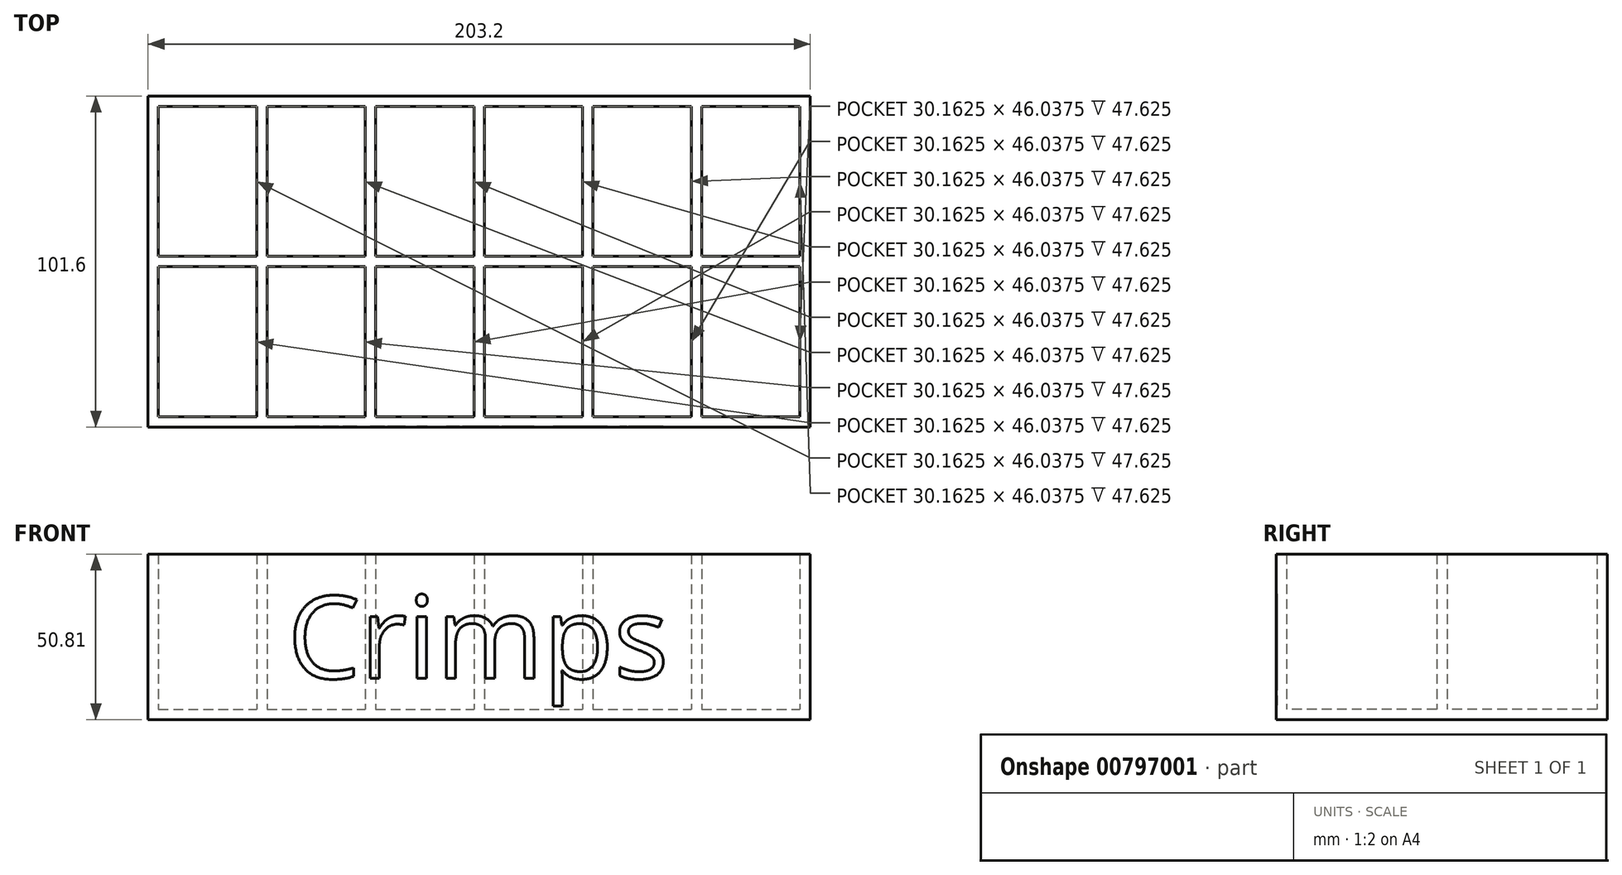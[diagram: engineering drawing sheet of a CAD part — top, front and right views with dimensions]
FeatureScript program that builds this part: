
annotation { "Feature Type Name" : "Feature", "Feature Type Description" : "" }
export const myFeature = defineFeature(function(context is Context, id is Id, definition is map)
    precondition{}
    {
        {
            var Q0;
            Q0=qCreatedBy(makeId("Top.planeOp"),FACE);
            var sketch = newSketch(context, id + "F0", { "sketchPlane" : qUnion([Q0])});
            skLineSegment(sketch, "E0.top", {"start": v(0, -101.6) * mm, "end": v(203.2, -101.6) * mm});
            skLineSegment(sketch, "E0.left", {"start": v(0, 0) * mm, "end": v(0, -101.6) * mm});
            skLineSegment(sketch, "E0.right", {"start": v(203.2, 0) * mm, "end": v(203.2, -101.6) * mm});
            skLineSegment(sketch, "E1.left", {"start": v(3.18, -3.17) * mm, "end": v(3.18, -49.21) * mm});
            skLineSegment(sketch, "E1.right", {"start": v(200.03, -3.17) * mm, "end": v(200.03, -98.43) * mm});
            skLineSegment(sketch, "E2", {"start": v(3.17, -3.17) * mm, "end": v(33.34, -3.17) * mm});
            skLineSegment(sketch, "E3", {"start": v(203.2, 0) * mm, "end": v(0, 0) * mm});
            skLineSegment(sketch, "E4", {"start": v(3.18, -98.43) * mm, "end": v(200.03, -98.43) * mm});
            skLineSegment(sketch, "E5.top", {"start": v(18.18, -98.43) * mm, "end": v(18.18, -98.43) * mm});
            skLineSegment(sketch, "E6", {"start": v(33.34, -98.43) * mm, "end": v(33.34, -52.39) * mm});
            skLineSegment(sketch, "E7", {"start": v(36.51, -3.17) * mm, "end": v(36.51, -3.17) * mm});
            skLineSegment(sketch, "E8", {"start": v(36.51, -3.17) * mm, "end": v(36.51, -49.21) * mm});
            skLineSegment(sketch, "E9", {"start": v(36.51, -3.18) * mm, "end": v(66.67, -3.18) * mm});
            skLineSegment(sketch, "E10", {"start": v(66.68, -98.42) * mm, "end": v(66.68, -3.18) * mm});
            skLineSegment(sketch, "E11", {"start": v(69.85, -3.18) * mm, "end": v(69.85, -49.21) * mm});
            skLineSegment(sketch, "E12", {"start": v(69.85, -3.17) * mm, "end": v(100.01, -3.17) * mm});
            skLineSegment(sketch, "E13", {"start": v(100.01, -3.17) * mm, "end": v(100.01, -98.42) * mm});
            skLineSegment(sketch, "E14", {"start": v(103.19, -3.17) * mm, "end": v(103.19, -49.21) * mm});
            skLineSegment(sketch, "E15", {"start": v(117.07, -3.17) * mm, "end": v(133.35, -3.17) * mm});
            skLineSegment(sketch, "E16", {"start": v(133.35, -3.17) * mm, "end": v(133.35, -98.42) * mm});
            skLineSegment(sketch, "E17", {"start": v(103.19, -3.17) * mm, "end": v(117.07, -3.17) * mm});
            skLineSegment(sketch, "E18", {"start": v(136.52, -3.17) * mm, "end": v(136.53, -49.21) * mm});
            skLineSegment(sketch, "E19", {"start": v(133.35, -3.17) * mm, "end": v(133.35, -3.17) * mm});
            skLineSegment(sketch, "E20", {"start": v(136.52, -3.17) * mm, "end": v(166.69, -3.17) * mm});
            skLineSegment(sketch, "E21", {"start": v(166.69, -3.17) * mm, "end": v(166.69, -98.42) * mm});
            skLineSegment(sketch, "E22", {"start": v(169.86, -3.17) * mm, "end": v(169.86, -49.21) * mm});
            skLineSegment(sketch, "E23", {"start": v(169.86, -3.17) * mm, "end": v(200.03, -3.17) * mm});
            skLineSegment(sketch, "E24", {"start": v(3.18, -49.21) * mm, "end": v(33.34, -49.21) * mm});
            skLineSegment(sketch, "E25", {"start": v(3.18, -52.39) * mm, "end": v(33.34, -52.39) * mm});
            skLineSegment(sketch, "E26", {"start": v(3.18, -49.21) * mm, "end": v(3.18, -52.39) * mm});
            skLineSegment(sketch, "E27", {"start": v(3.18, -52.39) * mm, "end": v(3.18, -98.43) * mm});
            skLineSegment(sketch, "E28", {"start": v(33.34, -49.21) * mm, "end": v(33.34, -3.17) * mm});
            skLineSegment(sketch, "E29", {"start": v(36.51, -49.21) * mm, "end": v(36.51, -49.21) * mm});
            skLineSegment(sketch, "E30", {"start": v(66.68, -52.39) * mm, "end": v(36.51, -52.39) * mm});
            skLineSegment(sketch, "E31", {"start": v(36.51, -49.21) * mm, "end": v(66.68, -49.21) * mm});
            skLineSegment(sketch, "E32", {"start": v(36.51, -52.39) * mm, "end": v(36.51, -98.43) * mm});
            skLineSegment(sketch, "E33", {"start": v(69.85, -49.21) * mm, "end": v(100.01, -49.21) * mm});
            skLineSegment(sketch, "E34", {"start": v(100.01, -52.39) * mm, "end": v(69.85, -52.39) * mm});
            skLineSegment(sketch, "E35", {"start": v(69.85, -52.39) * mm, "end": v(69.85, -52.39) * mm});
            skLineSegment(sketch, "E36", {"start": v(69.85, -52.39) * mm, "end": v(69.85, -98.42) * mm});
            skLineSegment(sketch, "E37", {"start": v(103.19, -49.21) * mm, "end": v(103.19, -49.21) * mm});
            skLineSegment(sketch, "E38", {"start": v(133.35, -52.39) * mm, "end": v(103.19, -52.39) * mm});
            skLineSegment(sketch, "E39", {"start": v(103.19, -49.21) * mm, "end": v(133.35, -49.21) * mm});
            skLineSegment(sketch, "E40", {"start": v(103.19, -52.39) * mm, "end": v(103.19, -98.42) * mm});
            skLineSegment(sketch, "E41", {"start": v(136.53, -49.21) * mm, "end": v(166.69, -49.21) * mm});
            skLineSegment(sketch, "E42", {"start": v(136.53, -52.39) * mm, "end": v(136.53, -52.39) * mm});
            skLineSegment(sketch, "E43", {"start": v(136.53, -52.39) * mm, "end": v(166.69, -52.39) * mm});
            skLineSegment(sketch, "E44", {"start": v(136.53, -52.39) * mm, "end": v(136.53, -98.42) * mm});
            skLineSegment(sketch, "E45", {"start": v(169.86, -49.21) * mm, "end": v(200.03, -49.21) * mm});
            skLineSegment(sketch, "E46", {"start": v(200.03, -52.39) * mm, "end": v(169.86, -52.39) * mm});
            skLineSegment(sketch, "E47", {"start": v(169.86, -52.39) * mm, "end": v(169.86, -98.42) * mm});
            skSolve(sketch);
        }
        {
            var Q0;
            Q0=makeQuery(id+"F0.imprint","IMPRINT",FACE,{"disambiguationData":[TD([[makeQuery(id+"F0.imprint","IMPRINT",EDGE,{"derivedFrom":sQuery(id+"F0.wireOp",EDGE,"E0.top")}),1.0]])]});
            var Q1;
            Q1=makeQuery(id+"F0.imprint","IMPRINT",FACE,{"disambiguationData":[TD([[makeQuery(id+"F0.imprint","IMPRINT",EDGE,{"derivedFrom":sQuery(id+"F0.wireOp",EDGE,"E5.bottom")}),-1.0]])]});
            var Q2;
            {var subQ0=sQuery(id+"F0.wireOp",EDGE,"646c8ae3-f2b2-429d-8022-bc64b3b6f105.1.0.0");Q2=makeQuery(id+"F0.imprint","IMPRINT",FACE,{"disambiguationData":[TD([[makeQuery(id+"F0.imprint","IMPRINT",EDGE,{"derivedFrom":subQ0}),1.0]])]});}
            var Q3;
            {var subQ0=sQuery(id+"F0.wireOp",EDGE,"646c8ae3-f2b2-429d-8022-bc64b3b6f105.2.0.0");Q3=makeQuery(id+"F0.imprint","IMPRINT",FACE,{"disambiguationData":[TD([[makeQuery(id+"F0.imprint","IMPRINT",EDGE,{"derivedFrom":subQ0}),1.0]])]});}
            var Q4;
            {var subQ0=sQuery(id+"F0.wireOp",EDGE,"646c8ae3-f2b2-429d-8022-bc64b3b6f105.3.0.0");Q4=makeQuery(id+"F0.imprint","IMPRINT",FACE,{"disambiguationData":[TD([[makeQuery(id+"F0.imprint","IMPRINT",EDGE,{"derivedFrom":subQ0}),1.0]])]});}
            var Q5;
            {var subQ0=sQuery(id+"F0.wireOp",EDGE,"646c8ae3-f2b2-429d-8022-bc64b3b6f105.4.0.0");Q5=makeQuery(id+"F0.imprint","IMPRINT",FACE,{"disambiguationData":[TD([[makeQuery(id+"F0.imprint","IMPRINT",EDGE,{"derivedFrom":subQ0}),1.0]])]});}
            var Q6;
            {var subQ0=sQuery(id+"F0.wireOp",EDGE,"646c8ae3-f2b2-429d-8022-bc64b3b6f105.5.0.0");Q6=makeQuery(id+"F0.imprint","IMPRINT",FACE,{"disambiguationData":[TD([[makeQuery(id+"F0.imprint","IMPRINT",EDGE,{"derivedFrom":subQ0}),1.0]])]});}
            var Q7;
            {var subQ0=sQuery(id+"F0.wireOp",EDGE,"646c8ae3-f2b2-429d-8022-bc64b3b6f105.6.0.0");Q7=makeQuery(id+"F0.imprint","IMPRINT",FACE,{"disambiguationData":[TD([[makeQuery(id+"F0.imprint","IMPRINT",EDGE,{"derivedFrom":subQ0}),1.0]])]});}
            var Q8;
            {var subQ0=sQuery(id+"F0.wireOp",EDGE,"646c8ae3-f2b2-429d-8022-bc64b3b6f105.7.0.0");Q8=makeQuery(id+"F0.imprint","IMPRINT",FACE,{"disambiguationData":[TD([[makeQuery(id+"F0.imprint","IMPRINT",EDGE,{"derivedFrom":subQ0}),1.0]])]});}
            var Q9;
            {var subQ0=sQuery(id+"F0.wireOp",EDGE,"646c8ae3-f2b2-429d-8022-bc64b3b6f105.8.0.0");Q9=makeQuery(id+"F0.imprint","IMPRINT",FACE,{"disambiguationData":[TD([[makeQuery(id+"F0.imprint","IMPRINT",EDGE,{"derivedFrom":subQ0}),1.0]])]});}
            var Q10;
            {var subQ0=sQuery(id+"F0.wireOp",EDGE,"646c8ae3-f2b2-429d-8022-bc64b3b6f105.9.0.0");Q10=makeQuery(id+"F0.imprint","IMPRINT",FACE,{"disambiguationData":[TD([[makeQuery(id+"F0.imprint","IMPRINT",EDGE,{"derivedFrom":subQ0}),1.0]])]});}
            extrude(context, id + "F1", {"entities" : qUnion([Q0, Q1, Q2, Q3, Q4, Q5, Q6, Q7, Q8, Q9, Q10]), "depth" : 47.62 * mm, "offsetDistance" : 25.4 * mm});
        }
        {
            var Q0;
            Q0=makeQuery(id+"FWKmPxKbktaoT75_1.boolean.opBoolean","MERGE",FACE,{"derivedFrom":[makeQuery(id+"F1.opExtrude","SWEPT_FACE",FACE,{"disambiguationData":[OSD([sQuery(id+"F0.wireOp",EDGE,"E0.top")])]}),makeQuery(id+"FWKmPxKbktaoT75_1.opExtrude","SWEPT_FACE",FACE,{"disambiguationData":[OSD([sQuery(id+"FPa2vzEjn9xWxvl_1.wireOp",EDGE,"pVME8pcI-fUVT-DpI0-aKQs-MaaHCtd98V99.bottom")])]})]});
            var sketch = newSketch(context, id + "F2", { "sketchPlane" : qUnion([Q0])});
            skText(sketch, "E48", { "text": "Crimps\n", "fontName": "OpenSans-Regular.ttf"});
            const initialGuessF2  = {"E48": [0.04284, 0.00952, 1, 0, 0.0254]};
            skSetInitialGuess(sketch, initialGuessF2);
            skSolve(sketch);
        }
        {
            var Q0;
            Q0 = qSketchRegion(id + "F2", true);
            extrude(context, id + "F3", {"entities" : qUnion([Q0]), "operationType" : NewBodyOperationType.REMOVE, "oppositeDirection" : true, "depth" : 0.25 * mm, "offsetDistance" : 25.4 * mm});
        }
        {
            var Q0;
            Q0=makeQuery(id+"F1.opExtrude","CAP_FACE",FACE,{"disambiguationData":[OSD([sQuery(id+"F0.wireOp",EDGE,"E0.top"),sQuery(id+"F0.wireOp",EDGE,"E0.left"),sQuery(id+"F0.wireOp",EDGE,"E0.right"),sQuery(id+"F0.wireOp",EDGE,"E1.left"),sQuery(id+"F0.wireOp",EDGE,"E1.right"),sQuery(id+"F0.wireOp",EDGE,"E2"),sQuery(id+"F0.wireOp",EDGE,"E3"),sQuery(id+"F0.wireOp",EDGE,"E4"),sQuery(id+"F0.wireOp",EDGE,"E6"),sQuery(id+"F0.wireOp",EDGE,"E8"),sQuery(id+"F0.wireOp",EDGE,"E9"),sQuery(id+"F0.wireOp",EDGE,"E10"),sQuery(id+"F0.wireOp",EDGE,"E11"),sQuery(id+"F0.wireOp",EDGE,"E12"),sQuery(id+"F0.wireOp",EDGE,"E13"),sQuery(id+"F0.wireOp",EDGE,"E14"),sQuery(id+"F0.wireOp",EDGE,"E15"),sQuery(id+"F0.wireOp",EDGE,"E16"),sQuery(id+"F0.wireOp",EDGE,"E17"),sQuery(id+"F0.wireOp",EDGE,"E18"),sQuery(id+"F0.wireOp",EDGE,"E20"),sQuery(id+"F0.wireOp",EDGE,"E21"),sQuery(id+"F0.wireOp",EDGE,"E22"),sQuery(id+"F0.wireOp",EDGE,"E23"),sQuery(id+"F0.wireOp",EDGE,"E24"),sQuery(id+"F0.wireOp",EDGE,"E25"),sQuery(id+"F0.wireOp",EDGE,"E27"),sQuery(id+"F0.wireOp",EDGE,"E28"),sQuery(id+"F0.wireOp",EDGE,"E30"),sQuery(id+"F0.wireOp",EDGE,"E31"),sQuery(id+"F0.wireOp",EDGE,"E32"),sQuery(id+"F0.wireOp",EDGE,"E33"),sQuery(id+"F0.wireOp",EDGE,"E34"),sQuery(id+"F0.wireOp",EDGE,"E36"),sQuery(id+"F0.wireOp",EDGE,"E38"),sQuery(id+"F0.wireOp",EDGE,"E39"),sQuery(id+"F0.wireOp",EDGE,"E40"),sQuery(id+"F0.wireOp",EDGE,"E41"),sQuery(id+"F0.wireOp",EDGE,"E43"),sQuery(id+"F0.wireOp",EDGE,"E44"),sQuery(id+"F0.wireOp",EDGE,"E45"),sQuery(id+"F0.wireOp",EDGE,"E46"),sQuery(id+"F0.wireOp",EDGE,"E47")])],"isStart":true});
            var sketch = newSketch(context, id + "F4", { "sketchPlane" : qUnion([Q0])});
            skLineSegment(sketch, "E49.bottom", {"start": v(0, 101.6) * mm, "end": v(203.2, 101.6) * mm});
            skLineSegment(sketch, "E49.top", {"start": v(0, 0) * mm, "end": v(203.2, 0) * mm});
            skLineSegment(sketch, "E49.left", {"start": v(0, 101.6) * mm, "end": v(0, 0) * mm});
            skLineSegment(sketch, "E49.right", {"start": v(203.2, 101.6) * mm, "end": v(203.2, 0) * mm});
            skSolve(sketch);
        }
        {
            var Q0;
            Q0 = qSketchRegion(id + "F4", true);
            extrude(context, id + "F5", {"entities" : qUnion([Q0]), "operationType" : NewBodyOperationType.ADD, "depth" : 3.17 * mm, "offsetDistance" : 25.4 * mm});
        }
    });
